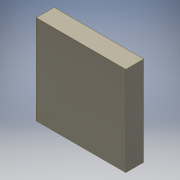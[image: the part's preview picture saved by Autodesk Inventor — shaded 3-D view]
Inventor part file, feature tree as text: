
AUTODESK INVENTOR PART (.ipt)
format: ipt  version: 2019.4 (Build 234330000, 330)  size: 98,304 bytes
history: native  units: mm
features: extrude x1, fillet x1, sketch x1
ambient origin geometry x8: Origin, YZ Plane, XZ Plane, XY Plane, X Axis, Y Axis, Z Axis, Center Point
bodies: Solid1 (feature_tree)
feature tree (3):
  extrude  "Extrusion1"  Depth=10.0mm
  fillet  "Fillet1"  Radius=2.0mm
  sketch  "Sketch1"  dims[d0=10.0mm d1=10.0mm d2=2.0mm d3=0.0mm d4=0.2mm]
